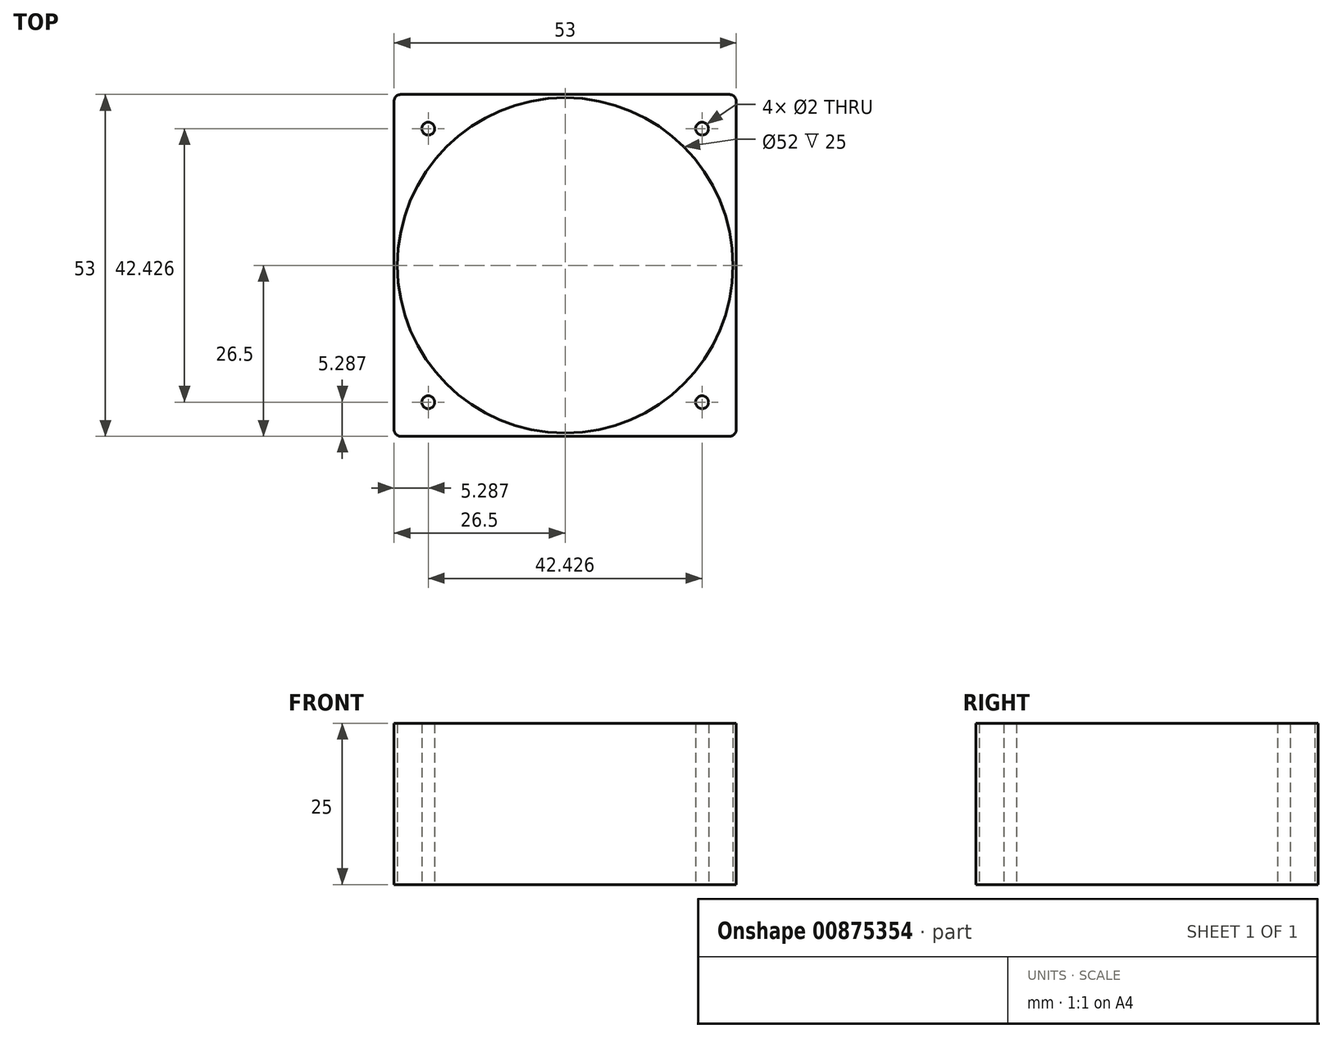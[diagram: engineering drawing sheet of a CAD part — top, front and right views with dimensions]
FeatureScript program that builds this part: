
annotation { "Feature Type Name" : "Feature", "Feature Type Description" : "" }
export const myFeature = defineFeature(function(context is Context, id is Id, definition is map)
    precondition{}
    {
        {
            var Q0;
            Q0=qCreatedBy(makeId("Top.planeOp"),FACE);
            var sketch = newSketch(context, id + "F0", { "sketchPlane" : qUnion([Q0])});
            skCircle(sketch, "E0", {"center": v(0, 0) * mm, "radius": 26 * mm});
            skLineSegment(sketch, "E1.bottom", {"start": v(26.5, -26.5) * mm, "end": v(-26.5, -26.5) * mm});
            skLineSegment(sketch, "E1.top", {"start": v(26.5, 26.5) * mm, "end": v(-26.5, 26.5) * mm});
            skLineSegment(sketch, "E1.left", {"start": v(26.5, -26.5) * mm, "end": v(26.5, 26.5) * mm});
            skLineSegment(sketch, "E1.right", {"start": v(-26.5, -26.5) * mm, "end": v(-26.5, 26.5) * mm});
            skCircle(sketch, "E2", {"center": v(0, -24.5) * mm, "radius": 1.5 * mm});
            skCircle(sketch, "E3", {"center": v(-21.21, 21.21) * mm, "radius": 1 * mm});
            skCircle(sketch, "E4", {"center": v(21.21, 21.21) * mm, "radius": 1 * mm});
            skCircle(sketch, "E5", {"center": v(21.21, -21.21) * mm, "radius": 1 * mm});
            skCircle(sketch, "E6", {"center": v(-21.21, -21.21) * mm, "radius": 1 * mm});
            skLineSegment(sketch, "E7", {"start": v(-26.5, 26.5) * mm, "end": v(26.5, -26.5) * mm, "construction": true});
            skLineSegment(sketch, "E8", {"start": v(26.5, 26.5) * mm, "end": v(-26.5, -26.5) * mm, "construction": true});
            skSolve(sketch);
        }
        {
            var Q0;
            Q0 = qSketchRegion(id + "F0", true);
            extrude(context, id + "F1", {"entities" : qUnion([Q0]), "depth" : 25 * mm, "offsetDistance" : 25 * mm});
        }
        {
            var Q0;
            Q0=makeQuery(id+"F1.opExtrude","SWEPT_EDGE",EDGE,{"disambiguationData":[OSD([sQuery(id+"F0.wireOp",EDGE,"E1.bottom"),sQuery(id+"F0.wireOp",EDGE,"E1.left")])]});
            var Q1;
            Q1=makeQuery(id+"F1.opExtrude","SWEPT_EDGE",EDGE,{"disambiguationData":[OSD([sQuery(id+"F0.wireOp",EDGE,"E1.top"),sQuery(id+"F0.wireOp",EDGE,"E1.left")])]});
            var Q2;
            Q2=makeQuery(id+"F1.opExtrude","SWEPT_EDGE",EDGE,{"disambiguationData":[OSD([sQuery(id+"F0.wireOp",EDGE,"E1.top"),sQuery(id+"F0.wireOp",EDGE,"E1.right")])]});
            var Q3;
            Q3=makeQuery(id+"F1.opExtrude","SWEPT_EDGE",EDGE,{"disambiguationData":[OSD([sQuery(id+"F0.wireOp",EDGE,"E1.bottom"),sQuery(id+"F0.wireOp",EDGE,"E1.right")])]});
            fillet(context, id + "F2", {"entities" : qUnion([Q0, Q1, Q2, Q3]), "radius" : 1 * mm, "tangentPropagation" : true, "allowEdgeOverflow" : false});
        }
    });
